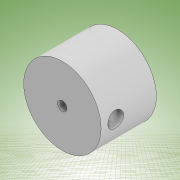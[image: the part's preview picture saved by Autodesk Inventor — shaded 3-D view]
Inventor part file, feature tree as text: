
AUTODESK INVENTOR PART (.ipt)
format: ipt  version: 2022 (Build 260153000, 153)  size: 146,432 bytes
history: native  units: mm
features: sketch x4, extrude x3, other x1, plane x1, hole x1
ambient origin geometry x8: Origin, YZ Plane, XZ Plane, XY Plane, X Axis, Y Axis, Z Axis, Center Point
bodies: Body1 (feature_tree)
feature tree (10):
  other  "Sólido1"
  extrude  "Extrusión1"  Depth=15.0mm TaperAngle=0.0deg
  extrude  "Extrusión2"  Depth=8.0mm TaperAngle=0.0deg
  extrude  "Extrusión3"  Depth=5.0mm TaperAngle=0.0deg
  plane  "Plano de trabajo1"
  hole  "Agujero1"  [1 undecoded]
  sketch  "Boceto1"  dims[d0=21.0mm d1=15.0mm d2=0.0mm]
  sketch  "Boceto2"  dims[d3=2.5mm d4=8.0mm d5=0.0mm]
  sketch  "Boceto3"  dims[d6=6.1mm d7=5.0mm d8=0.0mm]
  sketch  "Boceto4"  dims[d11=4.0mm d12=4.0mm d13=4.3mm d14=6.0mm d15=4.0mm d16=2.0mm d17=90.0deg d18=12.0mm d19=0.0mm]
note: 1 required parameter value undecoded (feature->parameter linkage not recoverable at this tier; creation-order binding heuristic only, values carry confidence <= 0.55)
